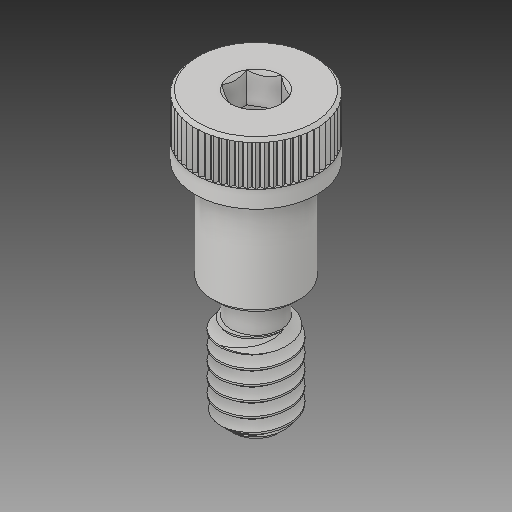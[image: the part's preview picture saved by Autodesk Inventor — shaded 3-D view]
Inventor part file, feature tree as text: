
AUTODESK INVENTOR PART (.ipt)
format: ipt  version: 2017 (Build 210142000, 142)  size: 594,432 bytes
history: mixed  units: in
note: dims shown in document units (in); Inventor stores cm internally (conversion verified against a paired STEP export)
features: chamfer x1, imported_body x1
ambient origin geometry x8: Origin, YZ Plane, XZ Plane, XY Plane, X Axis, Y Axis, Z Axis, Center Point
bodies: Solid1 (imported_parasolid)
feature tree (2):
  chamfer  "Chamfer3"  [1 undecoded]
  imported_body  NMx_Import_Brep_tag  [imported B-rep: ~22 faces, bbox_mm=[5.548635, 15.08125, 9.101667]]
note: 1 required parameter value undecoded (feature->parameter linkage not recoverable at this tier; creation-order binding heuristic only, values carry confidence <= 0.55)
